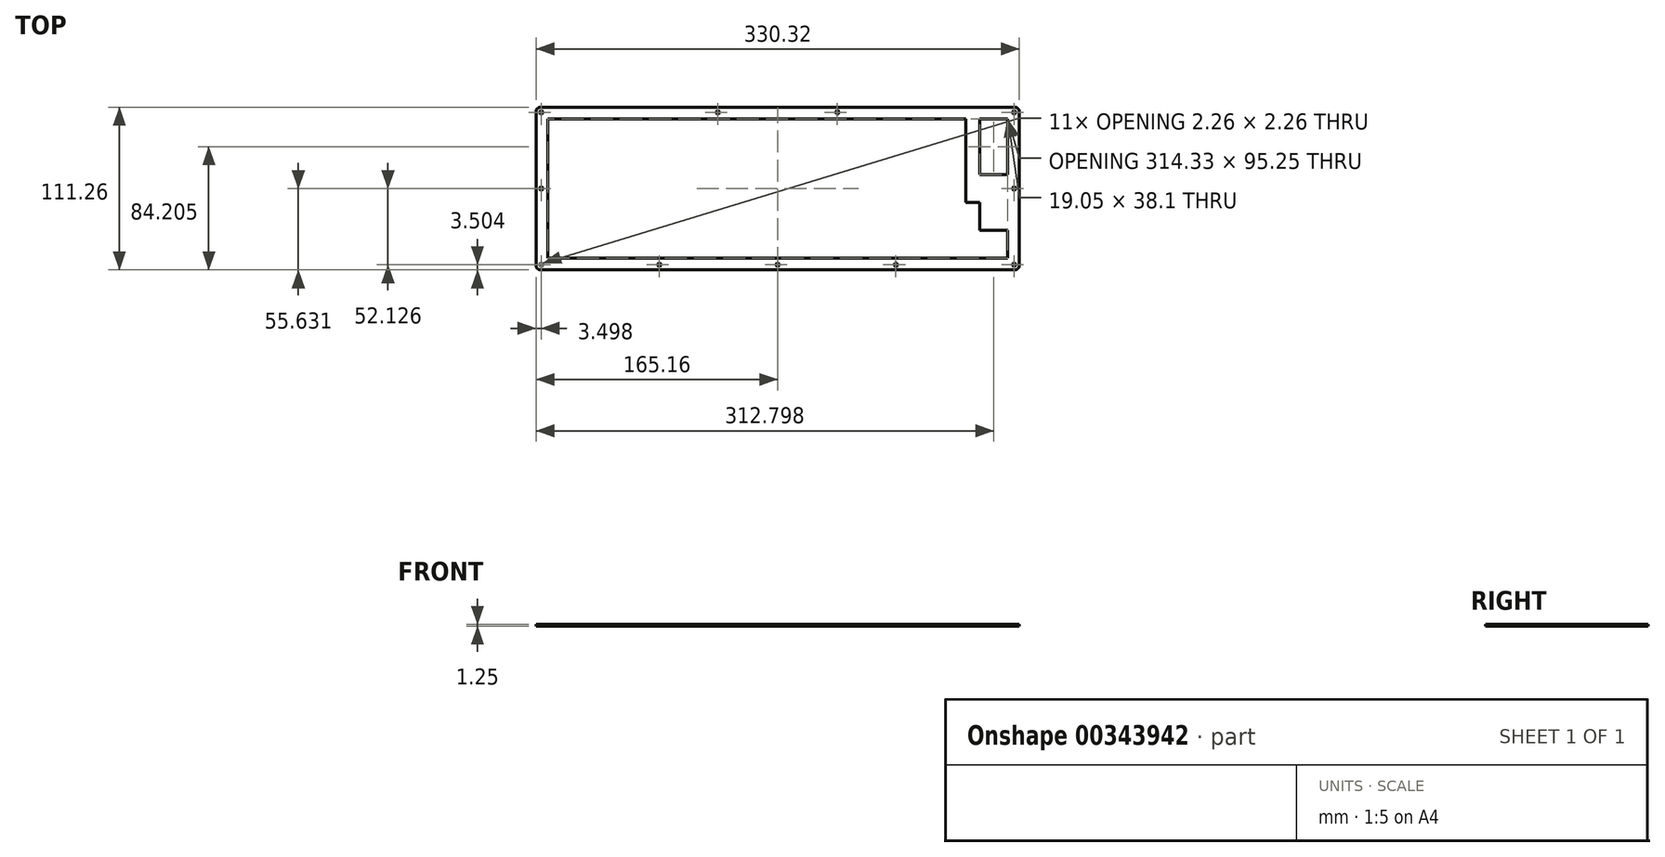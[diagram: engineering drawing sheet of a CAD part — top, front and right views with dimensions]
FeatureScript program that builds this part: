
annotation { "Feature Type Name" : "Feature", "Feature Type Description" : "" }
export const myFeature = defineFeature(function(context is Context, id is Id, definition is map)
    precondition{}
    {
        {
            var Q0;
            Q0=qCreatedBy(makeId("Top.planeOp"),FACE);
            var sketch = newSketch(context, id + "F0", { "sketchPlane" : qUnion([Q0])});
            skLineSegment(sketch, "E0", {"start": v(162.16, 55.62) * mm, "end": v(162.4, 55.62) * mm});
            skLineSegment(sketch, "E1", {"start": v(162.4, 55.62) * mm, "end": v(162.63, 55.59) * mm});
            skLineSegment(sketch, "E2", {"start": v(162.63, 55.59) * mm, "end": v(162.86, 55.54) * mm});
            skLineSegment(sketch, "E3", {"start": v(162.86, 55.54) * mm, "end": v(163.1, 55.48) * mm});
            skLineSegment(sketch, "E4", {"start": v(163.1, 55.48) * mm, "end": v(163.31, 55.4) * mm});
            skLineSegment(sketch, "E5", {"start": v(163.31, 55.4) * mm, "end": v(163.53, 55.3) * mm});
            skLineSegment(sketch, "E6", {"start": v(163.53, 55.3) * mm, "end": v(163.73, 55.18) * mm});
            skLineSegment(sketch, "E7", {"start": v(163.73, 55.18) * mm, "end": v(163.93, 55.05) * mm});
            skLineSegment(sketch, "E8", {"start": v(163.93, 55.05) * mm, "end": v(164.11, 54.9) * mm});
            skLineSegment(sketch, "E9", {"start": v(164.11, 54.9) * mm, "end": v(164.29, 54.75) * mm});
            skLineSegment(sketch, "E10", {"start": v(164.29, 54.75) * mm, "end": v(164.45, 54.57) * mm});
            skLineSegment(sketch, "E11", {"start": v(164.45, 54.57) * mm, "end": v(164.6, 54.39) * mm});
            skLineSegment(sketch, "E12", {"start": v(164.6, 54.39) * mm, "end": v(164.72, 54.2) * mm});
            skLineSegment(sketch, "E13", {"start": v(164.72, 54.2) * mm, "end": v(164.84, 53.99) * mm});
            skLineSegment(sketch, "E14", {"start": v(164.84, 53.99) * mm, "end": v(164.93, 53.77) * mm});
            skLineSegment(sketch, "E15", {"start": v(164.93, 53.77) * mm, "end": v(165.02, 53.55) * mm});
            skLineSegment(sketch, "E16", {"start": v(165.02, 53.55) * mm, "end": v(165.08, 53.33) * mm});
            skLineSegment(sketch, "E17", {"start": v(165.08, 53.33) * mm, "end": v(165.13, 53.1) * mm});
            skLineSegment(sketch, "E18", {"start": v(165.13, 53.1) * mm, "end": v(165.15, 52.86) * mm});
            skLineSegment(sketch, "E19", {"start": v(165.15, 52.86) * mm, "end": v(165.16, 52.62) * mm});
            skLineSegment(sketch, "E20", {"start": v(165.16, 52.62) * mm, "end": v(165.16, -52.63) * mm});
            skLineSegment(sketch, "E21", {"start": v(165.16, -52.63) * mm, "end": v(165.15, -52.86) * mm});
            skLineSegment(sketch, "E22", {"start": v(165.15, -52.86) * mm, "end": v(165.13, -53.1) * mm});
            skLineSegment(sketch, "E23", {"start": v(165.13, -53.1) * mm, "end": v(165.08, -53.33) * mm});
            skLineSegment(sketch, "E24", {"start": v(165.08, -53.33) * mm, "end": v(165.02, -53.55) * mm});
            skLineSegment(sketch, "E25", {"start": v(165.02, -53.55) * mm, "end": v(164.93, -53.77) * mm});
            skLineSegment(sketch, "E26", {"start": v(164.93, -53.77) * mm, "end": v(164.84, -53.99) * mm});
            skLineSegment(sketch, "E27", {"start": v(164.84, -53.99) * mm, "end": v(164.72, -54.2) * mm});
            skLineSegment(sketch, "E28", {"start": v(164.72, -54.2) * mm, "end": v(164.6, -54.39) * mm});
            skLineSegment(sketch, "E29", {"start": v(164.6, -54.39) * mm, "end": v(164.45, -54.57) * mm});
            skLineSegment(sketch, "E30", {"start": v(164.45, -54.57) * mm, "end": v(164.29, -54.75) * mm});
            skLineSegment(sketch, "E31", {"start": v(164.29, -54.75) * mm, "end": v(164.11, -54.9) * mm});
            skLineSegment(sketch, "E32", {"start": v(164.11, -54.9) * mm, "end": v(163.93, -55.05) * mm});
            skLineSegment(sketch, "E33", {"start": v(163.93, -55.05) * mm, "end": v(163.73, -55.18) * mm});
            skLineSegment(sketch, "E34", {"start": v(163.73, -55.18) * mm, "end": v(163.53, -55.3) * mm});
            skLineSegment(sketch, "E35", {"start": v(163.53, -55.3) * mm, "end": v(163.31, -55.4) * mm});
            skLineSegment(sketch, "E36", {"start": v(163.31, -55.4) * mm, "end": v(163.1, -55.48) * mm});
            skLineSegment(sketch, "E37", {"start": v(163.1, -55.48) * mm, "end": v(162.86, -55.54) * mm});
            skLineSegment(sketch, "E38", {"start": v(162.86, -55.54) * mm, "end": v(162.63, -55.59) * mm});
            skLineSegment(sketch, "E39", {"start": v(162.63, -55.59) * mm, "end": v(162.4, -55.62) * mm});
            skLineSegment(sketch, "E40", {"start": v(162.4, -55.62) * mm, "end": v(162.16, -55.63) * mm});
            skLineSegment(sketch, "E41", {"start": v(162.16, -55.63) * mm, "end": v(-162.16, -55.63) * mm});
            skLineSegment(sketch, "E42", {"start": v(-162.16, -55.63) * mm, "end": v(-162.4, -55.62) * mm});
            skLineSegment(sketch, "E43", {"start": v(-162.4, -55.62) * mm, "end": v(-162.63, -55.59) * mm});
            skLineSegment(sketch, "E44", {"start": v(-162.63, -55.59) * mm, "end": v(-162.86, -55.54) * mm});
            skLineSegment(sketch, "E45", {"start": v(-162.86, -55.54) * mm, "end": v(-163.09, -55.48) * mm});
            skLineSegment(sketch, "E46", {"start": v(-163.09, -55.48) * mm, "end": v(-163.31, -55.4) * mm});
            skLineSegment(sketch, "E47", {"start": v(-163.31, -55.4) * mm, "end": v(-163.52, -55.3) * mm});
            skLineSegment(sketch, "E48", {"start": v(-163.52, -55.3) * mm, "end": v(-163.73, -55.18) * mm});
            skLineSegment(sketch, "E49", {"start": v(-163.73, -55.18) * mm, "end": v(-163.93, -55.05) * mm});
            skLineSegment(sketch, "E50", {"start": v(-163.93, -55.05) * mm, "end": v(-164.11, -54.9) * mm});
            skLineSegment(sketch, "E51", {"start": v(-164.11, -54.9) * mm, "end": v(-164.28, -54.75) * mm});
            skLineSegment(sketch, "E52", {"start": v(-164.28, -54.75) * mm, "end": v(-164.44, -54.57) * mm});
            skLineSegment(sketch, "E53", {"start": v(-164.44, -54.57) * mm, "end": v(-164.6, -54.39) * mm});
            skLineSegment(sketch, "E54", {"start": v(-164.6, -54.39) * mm, "end": v(-164.72, -54.2) * mm});
            skLineSegment(sketch, "E55", {"start": v(-164.72, -54.2) * mm, "end": v(-164.84, -53.99) * mm});
            skLineSegment(sketch, "E56", {"start": v(-164.84, -53.99) * mm, "end": v(-164.93, -53.77) * mm});
            skLineSegment(sketch, "E57", {"start": v(-164.93, -53.77) * mm, "end": v(-165.02, -53.55) * mm});
            skLineSegment(sketch, "E58", {"start": v(-165.02, -53.55) * mm, "end": v(-165.08, -53.33) * mm});
            skLineSegment(sketch, "E59", {"start": v(-165.08, -53.33) * mm, "end": v(-165.13, -53.1) * mm});
            skLineSegment(sketch, "E60", {"start": v(-165.13, -53.1) * mm, "end": v(-165.15, -52.86) * mm});
            skLineSegment(sketch, "E61", {"start": v(-165.15, -52.86) * mm, "end": v(-165.16, -52.63) * mm});
            skLineSegment(sketch, "E62", {"start": v(-165.16, -52.63) * mm, "end": v(-165.16, 52.62) * mm});
            skLineSegment(sketch, "E63", {"start": v(-165.16, 52.62) * mm, "end": v(-165.15, 52.86) * mm});
            skLineSegment(sketch, "E64", {"start": v(-165.15, 52.86) * mm, "end": v(-165.13, 53.1) * mm});
            skLineSegment(sketch, "E65", {"start": v(-165.13, 53.1) * mm, "end": v(-165.08, 53.33) * mm});
            skLineSegment(sketch, "E66", {"start": v(-165.08, 53.33) * mm, "end": v(-165.02, 53.55) * mm});
            skLineSegment(sketch, "E67", {"start": v(-165.02, 53.55) * mm, "end": v(-164.93, 53.77) * mm});
            skLineSegment(sketch, "E68", {"start": v(-164.93, 53.77) * mm, "end": v(-164.84, 53.99) * mm});
            skLineSegment(sketch, "E69", {"start": v(-164.84, 53.99) * mm, "end": v(-164.72, 54.2) * mm});
            skLineSegment(sketch, "E70", {"start": v(-164.72, 54.2) * mm, "end": v(-164.6, 54.39) * mm});
            skLineSegment(sketch, "E71", {"start": v(-164.6, 54.39) * mm, "end": v(-164.44, 54.57) * mm});
            skLineSegment(sketch, "E72", {"start": v(-164.44, 54.57) * mm, "end": v(-164.28, 54.75) * mm});
            skLineSegment(sketch, "E73", {"start": v(-164.28, 54.75) * mm, "end": v(-164.11, 54.9) * mm});
            skLineSegment(sketch, "E74", {"start": v(-164.11, 54.9) * mm, "end": v(-163.93, 55.05) * mm});
            skLineSegment(sketch, "E75", {"start": v(-163.93, 55.05) * mm, "end": v(-163.73, 55.18) * mm});
            skLineSegment(sketch, "E76", {"start": v(-163.73, 55.18) * mm, "end": v(-163.52, 55.3) * mm});
            skLineSegment(sketch, "E77", {"start": v(-163.52, 55.3) * mm, "end": v(-163.31, 55.4) * mm});
            skLineSegment(sketch, "E78", {"start": v(-163.31, 55.4) * mm, "end": v(-163.09, 55.48) * mm});
            skLineSegment(sketch, "E79", {"start": v(-163.09, 55.48) * mm, "end": v(-162.86, 55.54) * mm});
            skLineSegment(sketch, "E80", {"start": v(-162.86, 55.54) * mm, "end": v(-162.63, 55.59) * mm});
            skLineSegment(sketch, "E81", {"start": v(-162.63, 55.59) * mm, "end": v(-162.4, 55.62) * mm});
            skLineSegment(sketch, "E82", {"start": v(-162.4, 55.62) * mm, "end": v(-162.16, 55.63) * mm});
            skLineSegment(sketch, "E83", {"start": v(-162.16, 55.63) * mm, "end": v(162.16, 55.62) * mm});
            skLineSegment(sketch, "E84", {"start": v(161.31, -51.05) * mm, "end": v(161, -51.21) * mm});
            skLineSegment(sketch, "E85", {"start": v(161, -51.21) * mm, "end": v(160.75, -51.46) * mm});
            skLineSegment(sketch, "E86", {"start": v(160.75, -51.46) * mm, "end": v(160.59, -51.78) * mm});
            skLineSegment(sketch, "E87", {"start": v(160.59, -51.78) * mm, "end": v(160.53, -52.13) * mm});
            skLineSegment(sketch, "E88", {"start": v(160.53, -52.13) * mm, "end": v(160.59, -52.48) * mm});
            skLineSegment(sketch, "E89", {"start": v(160.59, -52.48) * mm, "end": v(160.75, -52.79) * mm});
            skLineSegment(sketch, "E90", {"start": v(160.75, -52.79) * mm, "end": v(161, -53.04) * mm});
            skLineSegment(sketch, "E91", {"start": v(161, -53.04) * mm, "end": v(161.31, -53.2) * mm});
            skLineSegment(sketch, "E92", {"start": v(161.31, -53.2) * mm, "end": v(161.66, -53.26) * mm});
            skLineSegment(sketch, "E93", {"start": v(161.66, -53.26) * mm, "end": v(162.01, -53.2) * mm});
            skLineSegment(sketch, "E94", {"start": v(162.01, -53.2) * mm, "end": v(162.33, -53.04) * mm});
            skLineSegment(sketch, "E95", {"start": v(162.33, -53.04) * mm, "end": v(162.58, -52.79) * mm});
            skLineSegment(sketch, "E96", {"start": v(162.58, -52.79) * mm, "end": v(162.74, -52.48) * mm});
            skLineSegment(sketch, "E97", {"start": v(162.74, -52.48) * mm, "end": v(162.8, -52.13) * mm});
            skLineSegment(sketch, "E98", {"start": v(162.8, -52.13) * mm, "end": v(162.74, -51.78) * mm});
            skLineSegment(sketch, "E99", {"start": v(162.74, -51.78) * mm, "end": v(162.58, -51.46) * mm});
            skLineSegment(sketch, "E100", {"start": v(162.58, -51.46) * mm, "end": v(162.33, -51.21) * mm});
            skLineSegment(sketch, "E101", {"start": v(162.33, -51.21) * mm, "end": v(162.01, -51.05) * mm});
            skLineSegment(sketch, "E102", {"start": v(162.01, -51.05) * mm, "end": v(161.66, -51) * mm});
            skLineSegment(sketch, "E103", {"start": v(161.66, -51) * mm, "end": v(161.31, -51.05) * mm});
            skLineSegment(sketch, "E104", {"start": v(80.48, -51.05) * mm, "end": v(80.17, -51.21) * mm});
            skLineSegment(sketch, "E105", {"start": v(80.17, -51.21) * mm, "end": v(79.92, -51.46) * mm});
            skLineSegment(sketch, "E106", {"start": v(79.92, -51.46) * mm, "end": v(79.76, -51.78) * mm});
            skLineSegment(sketch, "E107", {"start": v(79.76, -51.78) * mm, "end": v(79.7, -52.13) * mm});
            skLineSegment(sketch, "E108", {"start": v(79.7, -52.13) * mm, "end": v(79.76, -52.48) * mm});
            skLineSegment(sketch, "E109", {"start": v(79.76, -52.48) * mm, "end": v(79.92, -52.79) * mm});
            skLineSegment(sketch, "E110", {"start": v(79.92, -52.79) * mm, "end": v(80.17, -53.04) * mm});
            skLineSegment(sketch, "E111", {"start": v(80.17, -53.04) * mm, "end": v(80.48, -53.2) * mm});
            skLineSegment(sketch, "E112", {"start": v(80.48, -53.2) * mm, "end": v(80.83, -53.26) * mm});
            skLineSegment(sketch, "E113", {"start": v(80.83, -53.26) * mm, "end": v(81.18, -53.2) * mm});
            skLineSegment(sketch, "E114", {"start": v(81.18, -53.2) * mm, "end": v(81.5, -53.04) * mm});
            skLineSegment(sketch, "E115", {"start": v(81.5, -53.04) * mm, "end": v(81.75, -52.79) * mm});
            skLineSegment(sketch, "E116", {"start": v(81.75, -52.79) * mm, "end": v(81.9, -52.48) * mm});
            skLineSegment(sketch, "E117", {"start": v(81.9, -52.48) * mm, "end": v(81.96, -52.13) * mm});
            skLineSegment(sketch, "E118", {"start": v(81.96, -52.13) * mm, "end": v(81.9, -51.78) * mm});
            skLineSegment(sketch, "E119", {"start": v(81.9, -51.78) * mm, "end": v(81.75, -51.46) * mm});
            skLineSegment(sketch, "E120", {"start": v(81.75, -51.46) * mm, "end": v(81.5, -51.21) * mm});
            skLineSegment(sketch, "E121", {"start": v(81.5, -51.21) * mm, "end": v(81.18, -51.05) * mm});
            skLineSegment(sketch, "E122", {"start": v(81.18, -51.05) * mm, "end": v(80.83, -51) * mm});
            skLineSegment(sketch, "E123", {"start": v(80.83, -51) * mm, "end": v(80.48, -51.05) * mm});
            skLineSegment(sketch, "E124", {"start": v(-0.35, -51.05) * mm, "end": v(-0.66, -51.21) * mm});
            skLineSegment(sketch, "E125", {"start": v(-0.66, -51.21) * mm, "end": v(-0.91, -51.46) * mm});
            skLineSegment(sketch, "E126", {"start": v(-0.91, -51.46) * mm, "end": v(-1.07, -51.78) * mm});
            skLineSegment(sketch, "E127", {"start": v(-1.07, -51.78) * mm, "end": v(-1.13, -52.13) * mm});
            skLineSegment(sketch, "E128", {"start": v(-1.13, -52.13) * mm, "end": v(-1.07, -52.48) * mm});
            skLineSegment(sketch, "E129", {"start": v(-1.07, -52.48) * mm, "end": v(-0.91, -52.79) * mm});
            skLineSegment(sketch, "E130", {"start": v(-0.91, -52.79) * mm, "end": v(-0.66, -53.04) * mm});
            skLineSegment(sketch, "E131", {"start": v(-0.66, -53.04) * mm, "end": v(-0.35, -53.2) * mm});
            skLineSegment(sketch, "E132", {"start": v(-0.35, -53.2) * mm, "end": v(0, -53.26) * mm});
            skLineSegment(sketch, "E133", {"start": v(0, -53.26) * mm, "end": v(0.35, -53.2) * mm});
            skLineSegment(sketch, "E134", {"start": v(0.35, -53.2) * mm, "end": v(0.67, -53.04) * mm});
            skLineSegment(sketch, "E135", {"start": v(0.67, -53.04) * mm, "end": v(0.92, -52.79) * mm});
            skLineSegment(sketch, "E136", {"start": v(0.92, -52.79) * mm, "end": v(1.07, -52.48) * mm});
            skLineSegment(sketch, "E137", {"start": v(1.07, -52.48) * mm, "end": v(1.13, -52.13) * mm});
            skLineSegment(sketch, "E138", {"start": v(1.13, -52.13) * mm, "end": v(1.07, -51.78) * mm});
            skLineSegment(sketch, "E139", {"start": v(1.07, -51.78) * mm, "end": v(0.92, -51.46) * mm});
            skLineSegment(sketch, "E140", {"start": v(0.92, -51.46) * mm, "end": v(0.67, -51.21) * mm});
            skLineSegment(sketch, "E141", {"start": v(0.67, -51.21) * mm, "end": v(0.35, -51.05) * mm});
            skLineSegment(sketch, "E142", {"start": v(0.35, -51.05) * mm, "end": v(0, -51) * mm});
            skLineSegment(sketch, "E143", {"start": v(0, -51) * mm, "end": v(-0.35, -51.05) * mm});
            skLineSegment(sketch, "E144", {"start": v(-81.18, -51.05) * mm, "end": v(-81.5, -51.21) * mm});
            skLineSegment(sketch, "E145", {"start": v(-81.5, -51.21) * mm, "end": v(-81.75, -51.46) * mm});
            skLineSegment(sketch, "E146", {"start": v(-81.75, -51.46) * mm, "end": v(-81.9, -51.78) * mm});
            skLineSegment(sketch, "E147", {"start": v(-81.9, -51.78) * mm, "end": v(-81.96, -52.13) * mm});
            skLineSegment(sketch, "E148", {"start": v(-81.96, -52.13) * mm, "end": v(-81.9, -52.48) * mm});
            skLineSegment(sketch, "E149", {"start": v(-81.9, -52.48) * mm, "end": v(-81.75, -52.79) * mm});
            skLineSegment(sketch, "E150", {"start": v(-81.75, -52.79) * mm, "end": v(-81.5, -53.04) * mm});
            skLineSegment(sketch, "E151", {"start": v(-81.5, -53.04) * mm, "end": v(-81.18, -53.2) * mm});
            skLineSegment(sketch, "E152", {"start": v(-81.18, -53.2) * mm, "end": v(-80.83, -53.26) * mm});
            skLineSegment(sketch, "E153", {"start": v(-80.83, -53.26) * mm, "end": v(-80.48, -53.2) * mm});
            skLineSegment(sketch, "E154", {"start": v(-80.48, -53.2) * mm, "end": v(-80.17, -53.04) * mm});
            skLineSegment(sketch, "E155", {"start": v(-80.17, -53.04) * mm, "end": v(-79.92, -52.79) * mm});
            skLineSegment(sketch, "E156", {"start": v(-79.92, -52.79) * mm, "end": v(-79.76, -52.48) * mm});
            skLineSegment(sketch, "E157", {"start": v(-79.76, -52.48) * mm, "end": v(-79.7, -52.13) * mm});
            skLineSegment(sketch, "E158", {"start": v(-79.7, -52.13) * mm, "end": v(-79.76, -51.78) * mm});
            skLineSegment(sketch, "E159", {"start": v(-79.76, -51.78) * mm, "end": v(-79.92, -51.46) * mm});
            skLineSegment(sketch, "E160", {"start": v(-79.92, -51.46) * mm, "end": v(-80.17, -51.21) * mm});
            skLineSegment(sketch, "E161", {"start": v(-80.17, -51.21) * mm, "end": v(-80.48, -51.05) * mm});
            skLineSegment(sketch, "E162", {"start": v(-80.48, -51.05) * mm, "end": v(-80.83, -51) * mm});
            skLineSegment(sketch, "E163", {"start": v(-80.83, -51) * mm, "end": v(-81.18, -51.05) * mm});
            skLineSegment(sketch, "E164", {"start": v(-162.01, -51.05) * mm, "end": v(-162.33, -51.21) * mm});
            skLineSegment(sketch, "E165", {"start": v(-162.33, -51.21) * mm, "end": v(-162.58, -51.46) * mm});
            skLineSegment(sketch, "E166", {"start": v(-162.58, -51.46) * mm, "end": v(-162.74, -51.78) * mm});
            skLineSegment(sketch, "E167", {"start": v(-162.74, -51.78) * mm, "end": v(-162.8, -52.13) * mm});
            skLineSegment(sketch, "E168", {"start": v(-162.8, -52.13) * mm, "end": v(-162.74, -52.48) * mm});
            skLineSegment(sketch, "E169", {"start": v(-162.74, -52.48) * mm, "end": v(-162.58, -52.79) * mm});
            skLineSegment(sketch, "E170", {"start": v(-162.58, -52.79) * mm, "end": v(-162.33, -53.04) * mm});
            skLineSegment(sketch, "E171", {"start": v(-162.33, -53.04) * mm, "end": v(-162.01, -53.2) * mm});
            skLineSegment(sketch, "E172", {"start": v(-162.01, -53.2) * mm, "end": v(-161.66, -53.26) * mm});
            skLineSegment(sketch, "E173", {"start": v(-161.66, -53.26) * mm, "end": v(-161.31, -53.2) * mm});
            skLineSegment(sketch, "E174", {"start": v(-161.31, -53.2) * mm, "end": v(-161, -53.04) * mm});
            skLineSegment(sketch, "E175", {"start": v(-161, -53.04) * mm, "end": v(-160.75, -52.79) * mm});
            skLineSegment(sketch, "E176", {"start": v(-160.75, -52.79) * mm, "end": v(-160.59, -52.48) * mm});
            skLineSegment(sketch, "E177", {"start": v(-160.59, -52.48) * mm, "end": v(-160.53, -52.13) * mm});
            skLineSegment(sketch, "E178", {"start": v(-160.53, -52.13) * mm, "end": v(-160.59, -51.78) * mm});
            skLineSegment(sketch, "E179", {"start": v(-160.59, -51.78) * mm, "end": v(-160.75, -51.46) * mm});
            skLineSegment(sketch, "E180", {"start": v(-160.75, -51.46) * mm, "end": v(-161, -51.21) * mm});
            skLineSegment(sketch, "E181", {"start": v(-161, -51.21) * mm, "end": v(-161.31, -51.05) * mm});
            skLineSegment(sketch, "E182", {"start": v(-161.31, -51.05) * mm, "end": v(-161.66, -51) * mm});
            skLineSegment(sketch, "E183", {"start": v(-161.66, -51) * mm, "end": v(-162.01, -51.05) * mm});
            skLineSegment(sketch, "E184", {"start": v(-157.16, 47.63) * mm, "end": v(-157.16, 28.57) * mm});
            skLineSegment(sketch, "E185", {"start": v(-157.16, 28.57) * mm, "end": v(-157.16, 28.57) * mm});
            skLineSegment(sketch, "E186", {"start": v(-157.16, 28.57) * mm, "end": v(-157.16, 9.53) * mm});
            skLineSegment(sketch, "E187", {"start": v(-157.16, 9.53) * mm, "end": v(-157.16, 9.53) * mm});
            skLineSegment(sketch, "E188", {"start": v(-157.16, 9.53) * mm, "end": v(-157.16, -9.53) * mm});
            skLineSegment(sketch, "E189", {"start": v(-157.16, -9.53) * mm, "end": v(-157.16, -9.53) * mm});
            skLineSegment(sketch, "E190", {"start": v(-157.16, -9.53) * mm, "end": v(-157.16, -47.62) * mm});
            skLineSegment(sketch, "E191", {"start": v(-157.16, -47.62) * mm, "end": v(157.16, -47.62) * mm});
            skLineSegment(sketch, "E192", {"start": v(157.16, -47.62) * mm, "end": v(157.16, -28.57) * mm});
            skLineSegment(sketch, "E193", {"start": v(157.16, -28.57) * mm, "end": v(138.11, -28.57) * mm});
            skLineSegment(sketch, "E194", {"start": v(138.11, -28.57) * mm, "end": v(138.11, -9.52) * mm});
            skLineSegment(sketch, "E195", {"start": v(138.11, -9.52) * mm, "end": v(128.59, -9.52) * mm});
            skLineSegment(sketch, "E196", {"start": v(128.59, -9.52) * mm, "end": v(128.59, 47.63) * mm});
            skLineSegment(sketch, "E197", {"start": v(128.59, 47.63) * mm, "end": v(-157.16, 47.63) * mm});
            skLineSegment(sketch, "E198", {"start": v(161.31, 1.08) * mm, "end": v(161, 0.91) * mm});
            skLineSegment(sketch, "E199", {"start": v(161, 0.91) * mm, "end": v(160.75, 0.66) * mm});
            skLineSegment(sketch, "E200", {"start": v(160.75, 0.66) * mm, "end": v(160.59, 0.35) * mm});
            skLineSegment(sketch, "E201", {"start": v(160.59, 0.35) * mm, "end": v(160.53, 0) * mm});
            skLineSegment(sketch, "E202", {"start": v(160.53, 0) * mm, "end": v(160.59, -0.35) * mm});
            skLineSegment(sketch, "E203", {"start": v(160.59, -0.35) * mm, "end": v(160.75, -0.66) * mm});
            skLineSegment(sketch, "E204", {"start": v(160.75, -0.66) * mm, "end": v(161, -0.91) * mm});
            skLineSegment(sketch, "E205", {"start": v(161, -0.91) * mm, "end": v(161.31, -1.07) * mm});
            skLineSegment(sketch, "E206", {"start": v(161.31, -1.07) * mm, "end": v(161.66, -1.13) * mm});
            skLineSegment(sketch, "E207", {"start": v(161.66, -1.13) * mm, "end": v(162.01, -1.07) * mm});
            skLineSegment(sketch, "E208", {"start": v(162.01, -1.07) * mm, "end": v(162.33, -0.91) * mm});
            skLineSegment(sketch, "E209", {"start": v(162.33, -0.91) * mm, "end": v(162.58, -0.66) * mm});
            skLineSegment(sketch, "E210", {"start": v(162.58, -0.66) * mm, "end": v(162.74, -0.35) * mm});
            skLineSegment(sketch, "E211", {"start": v(162.74, -0.35) * mm, "end": v(162.8, 0) * mm});
            skLineSegment(sketch, "E212", {"start": v(162.8, 0) * mm, "end": v(162.74, 0.35) * mm});
            skLineSegment(sketch, "E213", {"start": v(162.74, 0.35) * mm, "end": v(162.58, 0.66) * mm});
            skLineSegment(sketch, "E214", {"start": v(162.58, 0.66) * mm, "end": v(162.33, 0.91) * mm});
            skLineSegment(sketch, "E215", {"start": v(162.33, 0.91) * mm, "end": v(162.01, 1.08) * mm});
            skLineSegment(sketch, "E216", {"start": v(162.01, 1.08) * mm, "end": v(161.66, 1.13) * mm});
            skLineSegment(sketch, "E217", {"start": v(161.66, 1.13) * mm, "end": v(161.31, 1.08) * mm});
            skLineSegment(sketch, "E218", {"start": v(-162.01, 1.08) * mm, "end": v(-162.33, 0.91) * mm});
            skLineSegment(sketch, "E219", {"start": v(-162.33, 0.91) * mm, "end": v(-162.58, 0.66) * mm});
            skLineSegment(sketch, "E220", {"start": v(-162.58, 0.66) * mm, "end": v(-162.74, 0.35) * mm});
            skLineSegment(sketch, "E221", {"start": v(-162.74, 0.35) * mm, "end": v(-162.8, 0) * mm});
            skLineSegment(sketch, "E222", {"start": v(-162.8, 0) * mm, "end": v(-162.74, -0.35) * mm});
            skLineSegment(sketch, "E223", {"start": v(-162.74, -0.35) * mm, "end": v(-162.58, -0.66) * mm});
            skLineSegment(sketch, "E224", {"start": v(-162.58, -0.66) * mm, "end": v(-162.33, -0.91) * mm});
            skLineSegment(sketch, "E225", {"start": v(-162.33, -0.91) * mm, "end": v(-162.01, -1.07) * mm});
            skLineSegment(sketch, "E226", {"start": v(-162.01, -1.07) * mm, "end": v(-161.66, -1.13) * mm});
            skLineSegment(sketch, "E227", {"start": v(-161.66, -1.13) * mm, "end": v(-161.31, -1.07) * mm});
            skLineSegment(sketch, "E228", {"start": v(-161.31, -1.07) * mm, "end": v(-161, -0.91) * mm});
            skLineSegment(sketch, "E229", {"start": v(-161, -0.91) * mm, "end": v(-160.75, -0.66) * mm});
            skLineSegment(sketch, "E230", {"start": v(-160.75, -0.66) * mm, "end": v(-160.59, -0.35) * mm});
            skLineSegment(sketch, "E231", {"start": v(-160.59, -0.35) * mm, "end": v(-160.53, 0) * mm});
            skLineSegment(sketch, "E232", {"start": v(-160.53, 0) * mm, "end": v(-160.59, 0.35) * mm});
            skLineSegment(sketch, "E233", {"start": v(-160.59, 0.35) * mm, "end": v(-160.75, 0.66) * mm});
            skLineSegment(sketch, "E234", {"start": v(-160.75, 0.66) * mm, "end": v(-161, 0.91) * mm});
            skLineSegment(sketch, "E235", {"start": v(-161, 0.91) * mm, "end": v(-161.31, 1.08) * mm});
            skLineSegment(sketch, "E236", {"start": v(-161.31, 1.08) * mm, "end": v(-161.66, 1.13) * mm});
            skLineSegment(sketch, "E237", {"start": v(-161.66, 1.13) * mm, "end": v(-162.01, 1.08) * mm});
            skLineSegment(sketch, "E238", {"start": v(138.11, 47.63) * mm, "end": v(157.16, 47.63) * mm});
            skLineSegment(sketch, "E239", {"start": v(157.16, 47.63) * mm, "end": v(157.16, 9.52) * mm});
            skLineSegment(sketch, "E240", {"start": v(157.16, 9.52) * mm, "end": v(138.11, 9.52) * mm});
            skLineSegment(sketch, "E241", {"start": v(138.11, 9.52) * mm, "end": v(138.11, 47.63) * mm});
            skLineSegment(sketch, "E242", {"start": v(-41.18, 53.2) * mm, "end": v(-41.5, 53.04) * mm});
            skLineSegment(sketch, "E243", {"start": v(-41.5, 53.04) * mm, "end": v(-41.75, 52.8) * mm});
            skLineSegment(sketch, "E244", {"start": v(-41.75, 52.8) * mm, "end": v(-41.9, 52.47) * mm});
            skLineSegment(sketch, "E245", {"start": v(-41.9, 52.47) * mm, "end": v(-41.96, 52.12) * mm});
            skLineSegment(sketch, "E246", {"start": v(-41.96, 52.12) * mm, "end": v(-41.9, 51.78) * mm});
            skLineSegment(sketch, "E247", {"start": v(-41.9, 51.78) * mm, "end": v(-41.75, 51.46) * mm});
            skLineSegment(sketch, "E248", {"start": v(-41.75, 51.46) * mm, "end": v(-41.5, 51.21) * mm});
            skLineSegment(sketch, "E249", {"start": v(-41.5, 51.21) * mm, "end": v(-41.18, 51.05) * mm});
            skLineSegment(sketch, "E250", {"start": v(-41.18, 51.05) * mm, "end": v(-40.83, 51) * mm});
            skLineSegment(sketch, "E251", {"start": v(-40.83, 51) * mm, "end": v(-40.48, 51.05) * mm});
            skLineSegment(sketch, "E252", {"start": v(-40.48, 51.05) * mm, "end": v(-40.17, 51.21) * mm});
            skLineSegment(sketch, "E253", {"start": v(-40.17, 51.21) * mm, "end": v(-39.92, 51.46) * mm});
            skLineSegment(sketch, "E254", {"start": v(-39.92, 51.46) * mm, "end": v(-39.76, 51.78) * mm});
            skLineSegment(sketch, "E255", {"start": v(-39.76, 51.78) * mm, "end": v(-39.7, 52.12) * mm});
            skLineSegment(sketch, "E256", {"start": v(-39.7, 52.12) * mm, "end": v(-39.76, 52.47) * mm});
            skLineSegment(sketch, "E257", {"start": v(-39.76, 52.47) * mm, "end": v(-39.92, 52.8) * mm});
            skLineSegment(sketch, "E258", {"start": v(-39.92, 52.8) * mm, "end": v(-40.17, 53.04) * mm});
            skLineSegment(sketch, "E259", {"start": v(-40.17, 53.04) * mm, "end": v(-40.48, 53.2) * mm});
            skLineSegment(sketch, "E260", {"start": v(-40.48, 53.2) * mm, "end": v(-40.83, 53.26) * mm});
            skLineSegment(sketch, "E261", {"start": v(-40.83, 53.26) * mm, "end": v(-41.18, 53.2) * mm});
            skLineSegment(sketch, "E262", {"start": v(40.48, 53.2) * mm, "end": v(40.17, 53.04) * mm});
            skLineSegment(sketch, "E263", {"start": v(40.17, 53.04) * mm, "end": v(39.92, 52.8) * mm});
            skLineSegment(sketch, "E264", {"start": v(39.92, 52.8) * mm, "end": v(39.76, 52.47) * mm});
            skLineSegment(sketch, "E265", {"start": v(39.76, 52.47) * mm, "end": v(39.7, 52.12) * mm});
            skLineSegment(sketch, "E266", {"start": v(39.7, 52.12) * mm, "end": v(39.76, 51.78) * mm});
            skLineSegment(sketch, "E267", {"start": v(39.76, 51.78) * mm, "end": v(39.92, 51.46) * mm});
            skLineSegment(sketch, "E268", {"start": v(39.92, 51.46) * mm, "end": v(40.17, 51.21) * mm});
            skLineSegment(sketch, "E269", {"start": v(40.17, 51.21) * mm, "end": v(40.48, 51.05) * mm});
            skLineSegment(sketch, "E270", {"start": v(40.48, 51.05) * mm, "end": v(40.83, 51) * mm});
            skLineSegment(sketch, "E271", {"start": v(40.83, 51) * mm, "end": v(41.18, 51.05) * mm});
            skLineSegment(sketch, "E272", {"start": v(41.18, 51.05) * mm, "end": v(41.5, 51.21) * mm});
            skLineSegment(sketch, "E273", {"start": v(41.5, 51.21) * mm, "end": v(41.75, 51.46) * mm});
            skLineSegment(sketch, "E274", {"start": v(41.75, 51.46) * mm, "end": v(41.9, 51.78) * mm});
            skLineSegment(sketch, "E275", {"start": v(41.9, 51.78) * mm, "end": v(41.96, 52.12) * mm});
            skLineSegment(sketch, "E276", {"start": v(41.96, 52.12) * mm, "end": v(41.9, 52.47) * mm});
            skLineSegment(sketch, "E277", {"start": v(41.9, 52.47) * mm, "end": v(41.75, 52.8) * mm});
            skLineSegment(sketch, "E278", {"start": v(41.75, 52.8) * mm, "end": v(41.5, 53.04) * mm});
            skLineSegment(sketch, "E279", {"start": v(41.5, 53.04) * mm, "end": v(41.18, 53.2) * mm});
            skLineSegment(sketch, "E280", {"start": v(41.18, 53.2) * mm, "end": v(40.83, 53.26) * mm});
            skLineSegment(sketch, "E281", {"start": v(40.83, 53.26) * mm, "end": v(40.48, 53.2) * mm});
            skLineSegment(sketch, "E282", {"start": v(161.31, 53.2) * mm, "end": v(161, 53.04) * mm});
            skLineSegment(sketch, "E283", {"start": v(161, 53.04) * mm, "end": v(160.75, 52.8) * mm});
            skLineSegment(sketch, "E284", {"start": v(160.75, 52.8) * mm, "end": v(160.59, 52.47) * mm});
            skLineSegment(sketch, "E285", {"start": v(160.59, 52.47) * mm, "end": v(160.53, 52.12) * mm});
            skLineSegment(sketch, "E286", {"start": v(160.53, 52.12) * mm, "end": v(160.59, 51.78) * mm});
            skLineSegment(sketch, "E287", {"start": v(160.59, 51.78) * mm, "end": v(160.75, 51.46) * mm});
            skLineSegment(sketch, "E288", {"start": v(160.75, 51.46) * mm, "end": v(161, 51.21) * mm});
            skLineSegment(sketch, "E289", {"start": v(161, 51.21) * mm, "end": v(161.31, 51.05) * mm});
            skLineSegment(sketch, "E290", {"start": v(161.31, 51.05) * mm, "end": v(161.66, 51) * mm});
            skLineSegment(sketch, "E291", {"start": v(161.66, 51) * mm, "end": v(162.01, 51.05) * mm});
            skLineSegment(sketch, "E292", {"start": v(162.01, 51.05) * mm, "end": v(162.33, 51.21) * mm});
            skLineSegment(sketch, "E293", {"start": v(162.33, 51.21) * mm, "end": v(162.58, 51.46) * mm});
            skLineSegment(sketch, "E294", {"start": v(162.58, 51.46) * mm, "end": v(162.74, 51.78) * mm});
            skLineSegment(sketch, "E295", {"start": v(162.74, 51.78) * mm, "end": v(162.8, 52.12) * mm});
            skLineSegment(sketch, "E296", {"start": v(162.8, 52.12) * mm, "end": v(162.74, 52.47) * mm});
            skLineSegment(sketch, "E297", {"start": v(162.74, 52.47) * mm, "end": v(162.58, 52.8) * mm});
            skLineSegment(sketch, "E298", {"start": v(162.58, 52.8) * mm, "end": v(162.33, 53.04) * mm});
            skLineSegment(sketch, "E299", {"start": v(162.33, 53.04) * mm, "end": v(162.01, 53.2) * mm});
            skLineSegment(sketch, "E300", {"start": v(162.01, 53.2) * mm, "end": v(161.66, 53.26) * mm});
            skLineSegment(sketch, "E301", {"start": v(161.66, 53.26) * mm, "end": v(161.31, 53.2) * mm});
            skLineSegment(sketch, "E302", {"start": v(-162.01, 53.2) * mm, "end": v(-162.33, 53.04) * mm});
            skLineSegment(sketch, "E303", {"start": v(-162.33, 53.04) * mm, "end": v(-162.58, 52.8) * mm});
            skLineSegment(sketch, "E304", {"start": v(-162.58, 52.8) * mm, "end": v(-162.74, 52.47) * mm});
            skLineSegment(sketch, "E305", {"start": v(-162.74, 52.47) * mm, "end": v(-162.8, 52.12) * mm});
            skLineSegment(sketch, "E306", {"start": v(-162.8, 52.12) * mm, "end": v(-162.74, 51.78) * mm});
            skLineSegment(sketch, "E307", {"start": v(-162.74, 51.78) * mm, "end": v(-162.58, 51.46) * mm});
            skLineSegment(sketch, "E308", {"start": v(-162.58, 51.46) * mm, "end": v(-162.33, 51.21) * mm});
            skLineSegment(sketch, "E309", {"start": v(-162.33, 51.21) * mm, "end": v(-162.01, 51.05) * mm});
            skLineSegment(sketch, "E310", {"start": v(-162.01, 51.05) * mm, "end": v(-161.66, 51) * mm});
            skLineSegment(sketch, "E311", {"start": v(-161.66, 51) * mm, "end": v(-161.31, 51.05) * mm});
            skLineSegment(sketch, "E312", {"start": v(-161.31, 51.05) * mm, "end": v(-161, 51.21) * mm});
            skLineSegment(sketch, "E313", {"start": v(-161, 51.21) * mm, "end": v(-160.75, 51.46) * mm});
            skLineSegment(sketch, "E314", {"start": v(-160.75, 51.46) * mm, "end": v(-160.59, 51.78) * mm});
            skLineSegment(sketch, "E315", {"start": v(-160.59, 51.78) * mm, "end": v(-160.53, 52.12) * mm});
            skLineSegment(sketch, "E316", {"start": v(-160.53, 52.12) * mm, "end": v(-160.59, 52.47) * mm});
            skLineSegment(sketch, "E317", {"start": v(-160.59, 52.47) * mm, "end": v(-160.75, 52.8) * mm});
            skLineSegment(sketch, "E318", {"start": v(-160.75, 52.8) * mm, "end": v(-161, 53.04) * mm});
            skLineSegment(sketch, "E319", {"start": v(-161, 53.04) * mm, "end": v(-161.31, 53.2) * mm});
            skLineSegment(sketch, "E320", {"start": v(-161.31, 53.2) * mm, "end": v(-161.66, 53.26) * mm});
            skLineSegment(sketch, "E321", {"start": v(-161.66, 53.26) * mm, "end": v(-162.01, 53.2) * mm});
            skSolve(sketch);
        }
        {
            var Q0;
            Q0 = qSketchRegion(id + "F0", true);
            extrude(context, id + "F1", {"entities" : qUnion([Q0]), "depth" : 1.25 * mm});
        }
    });
